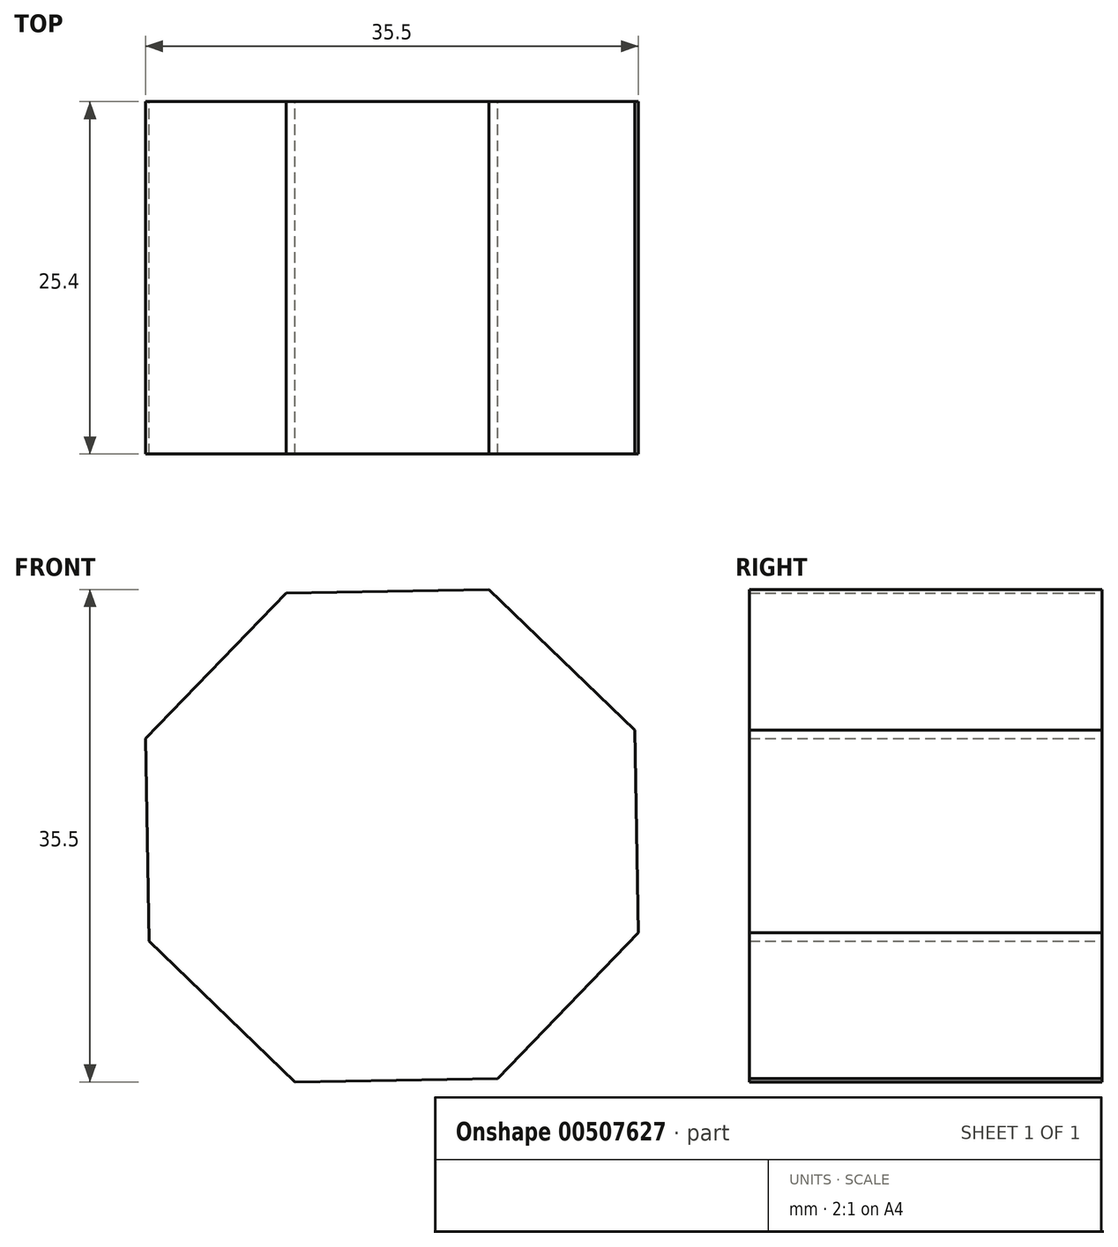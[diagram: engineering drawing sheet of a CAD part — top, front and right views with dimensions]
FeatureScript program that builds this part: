
annotation { "Feature Type Name" : "Feature", "Feature Type Description" : "" }
export const myFeature = defineFeature(function(context is Context, id is Id, definition is map)
    precondition{}
    {
        {
            var Q0;
            Q0=qCreatedBy(makeId("Front.planeOp"),FACE);
            var sketch = newSketch(context, id + "F0", { "sketchPlane" : qUnion([Q0])});
            skCircle(sketch, "E0.cCircle", {"center": v(0, 0) * mm, "radius": 17.62 * mm, "construction": true});
            skLineSegment(sketch, "E0.0", {"start": v(-7, -17.75) * mm, "end": v(-17.5, -7.6) * mm});
            skLineSegment(sketch, "E0.1", {"start": v(-17.5, -7.6) * mm, "end": v(-17.75, 7) * mm});
            skLineSegment(sketch, "E0.2", {"start": v(-17.75, 7) * mm, "end": v(-7.6, 17.5) * mm});
            skLineSegment(sketch, "E0.3", {"start": v(-7.6, 17.5) * mm, "end": v(7, 17.75) * mm});
            skLineSegment(sketch, "E0.4", {"start": v(7, 17.75) * mm, "end": v(17.5, 7.6) * mm});
            skLineSegment(sketch, "E0.5", {"start": v(17.5, 7.6) * mm, "end": v(17.75, -7) * mm});
            skLineSegment(sketch, "E0.6", {"start": v(17.75, -7) * mm, "end": v(7.6, -17.5) * mm});
            skLineSegment(sketch, "E0.7", {"start": v(7.6, -17.5) * mm, "end": v(-7, -17.75) * mm});
            skPoint(sketch, "E0.0.midPoint", {"position": v(-12.24, -12.68) * mm});
            skSolve(sketch);
        }
        {
            var Q0;
            Q0=makeQuery(id+"F0.imprint","IMPRINT",FACE,{"disambiguationData":[TD([[makeQuery(id+"F0.imprint","IMPRINT",EDGE,{"derivedFrom":sQuery(id+"F0.wireOp",EDGE,"E0.0")}),-1.0]])]});
            extrude(context, id + "F1", {"entities" : qUnion([Q0]), "endBound" : BoundingType.SYMMETRIC, "depth" : 25.4 * mm});
        }
    });
